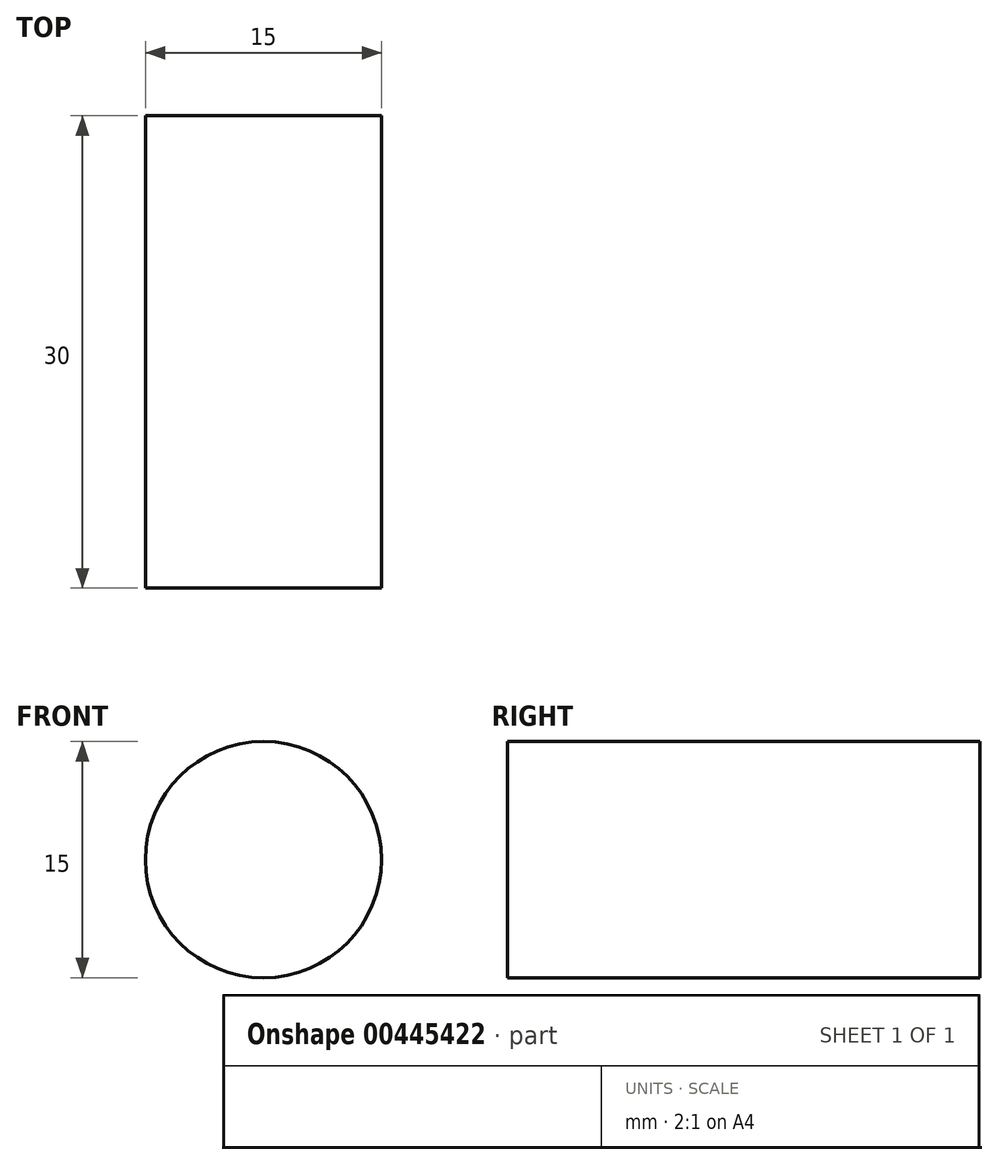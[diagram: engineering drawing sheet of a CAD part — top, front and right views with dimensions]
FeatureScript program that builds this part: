
annotation { "Feature Type Name" : "Feature", "Feature Type Description" : "" }
export const myFeature = defineFeature(function(context is Context, id is Id, definition is map)
    precondition{}
    {
        {
            var Q0;
            Q0=qCreatedBy(makeId("Front.planeOp"),FACE);
            var sketch = newSketch(context, id + "F0", { "sketchPlane" : qUnion([Q0])});
            skCircle(sketch, "E0", {"center": v(0, 0) * mm, "radius": 7.5 * mm});
            skSolve(sketch);
        }
        {
            var Q0;
            Q0=makeQuery(id+"F0.imprint","IMPRINT",FACE,{"disambiguationData":[TD([[makeQuery(id+"F0.imprint","IMPRINT",EDGE,{"derivedFrom":sQuery(id+"F0.wireOp",EDGE,"E0")}),1.0]])]});
            extrude(context, id + "F1", {"entities" : qUnion([Q0]), "depth" : 30 * mm});
        }
    });
